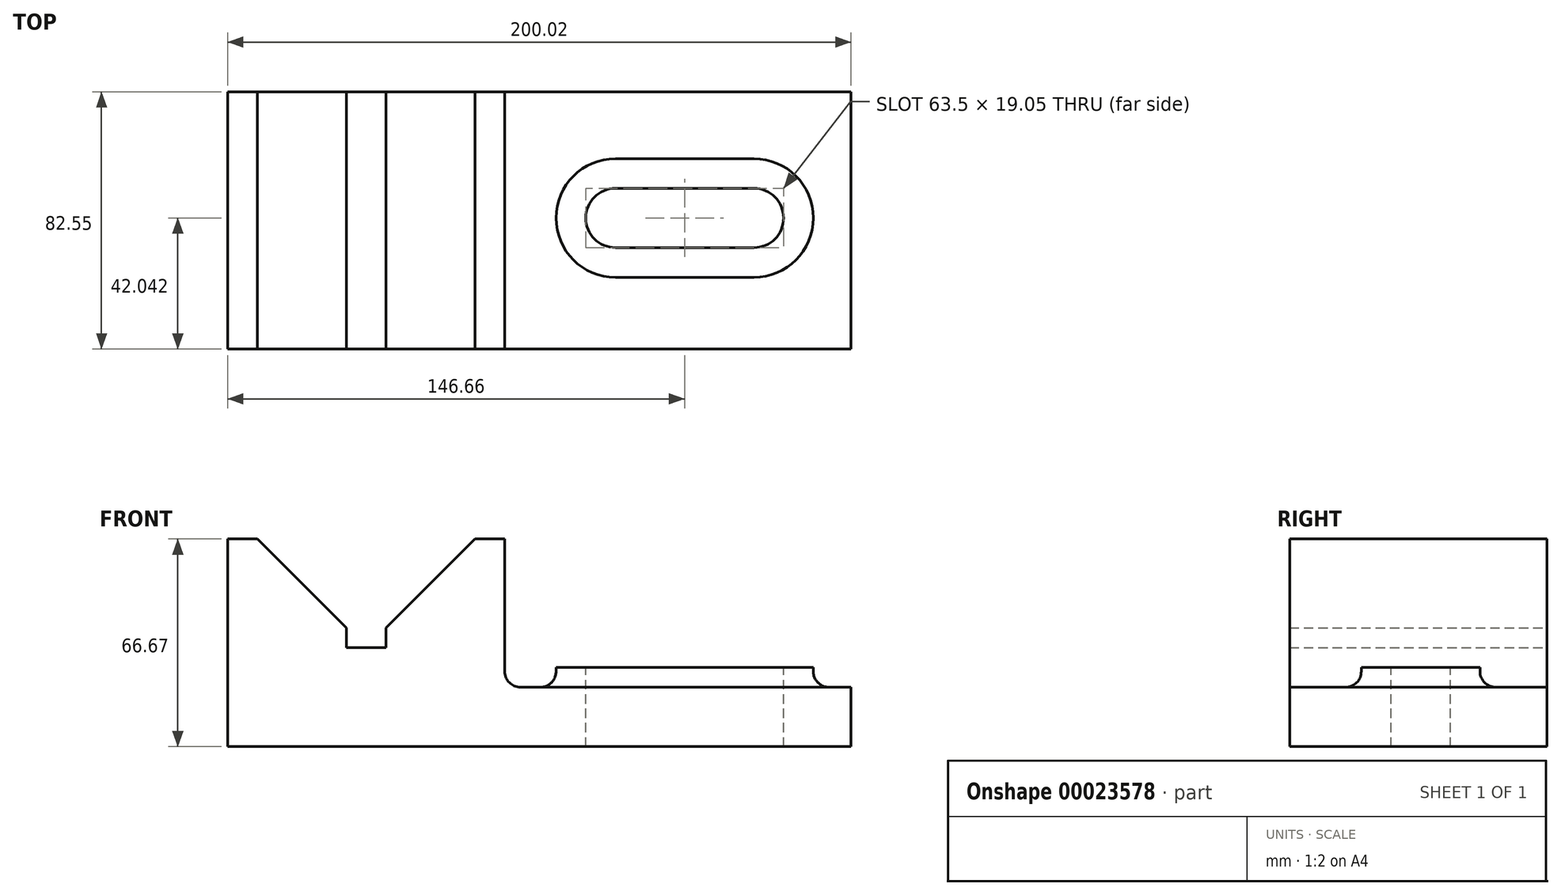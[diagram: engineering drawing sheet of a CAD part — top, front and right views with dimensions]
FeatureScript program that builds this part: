
annotation { "Feature Type Name" : "Feature", "Feature Type Description" : "" }
export const myFeature = defineFeature(function(context is Context, id is Id, definition is map)
    precondition{}
    {
        {
            var Q0;
            Q0=qCreatedBy(makeId("Front.planeOp"),FACE);
            var sketch = newSketch(context, id + "F0", { "sketchPlane" : qUnion([Q0])});
            skLineSegment(sketch, "E0.bottom", {"start": v(-75.58, -32.42) * mm, "end": v(124.44, -32.42) * mm});
            skLineSegment(sketch, "E0.top", {"start": v(-75.58, -51.47) * mm, "end": v(124.44, -51.47) * mm});
            skLineSegment(sketch, "E0.left", {"start": v(-75.58, -32.42) * mm, "end": v(-75.58, -51.47) * mm});
            skLineSegment(sketch, "E0.right", {"start": v(124.44, -32.42) * mm, "end": v(124.44, -51.47) * mm});
            skLineSegment(sketch, "E1.bottom", {"start": v(-75.58, -32.42) * mm, "end": v(-75.58, -32.42) * mm});
            skLineSegment(sketch, "E1.top", {"start": v(-75.58, -51.47) * mm, "end": v(-75.58, -51.47) * mm});
            skLineSegment(sketch, "E2.bottom", {"start": v(-75.58, -51.47) * mm, "end": v(13.32, -51.47) * mm});
            skLineSegment(sketch, "E2.left", {"start": v(-75.58, -51.47) * mm, "end": v(-75.58, 15.2) * mm});
            skLineSegment(sketch, "E2.right", {"start": v(13.32, -51.47) * mm, "end": v(13.32, 15.2) * mm});
            skLineSegment(sketch, "E3", {"start": v(-66.06, 15.2) * mm, "end": v(-37.48, -13.37) * mm});
            skLineSegment(sketch, "E4", {"start": v(-37.48, -13.37) * mm, "end": v(-37.48, -19.72) * mm});
            skLineSegment(sketch, "E5", {"start": v(-37.48, -19.72) * mm, "end": v(-24.78, -19.72) * mm});
            skLineSegment(sketch, "E6", {"start": v(-24.78, -19.72) * mm, "end": v(-24.78, -13.37) * mm});
            skLineSegment(sketch, "E7", {"start": v(-24.78, -13.37) * mm, "end": v(3.8, 15.2) * mm});
            skLineSegment(sketch, "E8.trimOffspring", {"start": v(3.8, 15.2) * mm, "end": v(13.32, 15.2) * mm});
            skLineSegment(sketch, "E9", {"start": v(-75.58, 15.2) * mm, "end": v(-66.06, 15.2) * mm});
            skSolve(sketch);
        }
        {
            var Q0;
            Q0 = qSketchRegion(id + "F0", true);
            extrude(context, id + "F1", {"entities" : qUnion([Q0]), "depth" : 82.55 * mm});
        }
        {
            var Q0;
            Q0=qCreatedBy(makeId("Top.planeOp"),FACE);
            var sketch = newSketch(context, id + "F2", { "sketchPlane" : qUnion([Q0])});
            skLineSegment(sketch, "E10.bottom", {"start": v(48.86, -30.98) * mm, "end": v(93.3, -30.98) * mm});
            skLineSegment(sketch, "E10.top", {"start": v(48.86, -50.03) * mm, "end": v(93.3, -50.03) * mm});
            skArc(sketch, "E11", {"start": v(48.86, -30.98) * mm, "mid": v(39.33, -40.5) * mm, "end": v(48.86, -50.03) * mm});
            skArc(sketch, "E12", {"start": v(93.3, -50.03) * mm, "mid": v(102.83, -40.5) * mm, "end": v(93.3, -30.98) * mm});
            skLineSegment(sketch, "E13.bottom", {"start": v(48.86, -59.56) * mm, "end": v(93.3, -59.56) * mm});
            skArc(sketch, "E14", {"start": v(93.3, -59.56) * mm, "mid": v(112.36, -40.5) * mm, "end": v(93.3, -21.46) * mm});
            skArc(sketch, "E15", {"start": v(48.86, -21.46) * mm, "mid": v(29.8, -40.5) * mm, "end": v(48.86, -59.56) * mm});
            skLineSegment(sketch, "E16", {"start": v(48.86, -21.46) * mm, "end": v(93.3, -21.46) * mm});
            skSolve(sketch);
        }
        {
            var Q0;
            Q0=makeQuery(id+"F2.imprint","IMPRINT",FACE,{"disambiguationData":[TD([[makeQuery(id+"F2.imprint","IMPRINT",EDGE,{"derivedFrom":sQuery(id+"F2.wireOp",EDGE,"E10.bottom")}),1.0]])]});
            extrude(context, id + "F3", {"entities" : qUnion([Q0]), "operationType" : NewBodyOperationType.ADD, "oppositeDirection" : true, "depth" : 38.1 * mm});
        }
        {
            var Q0;
            Q0=makeQuery(id+"F3.opExtrude","CAP_FACE",FACE,{"disambiguationData":[OSD([sQuery(id+"F2.wireOp",EDGE,"E10.bottom"),sQuery(id+"F2.wireOp",EDGE,"E10.top"),sQuery(id+"F2.wireOp",EDGE,"E11"),sQuery(id+"F2.wireOp",EDGE,"E12"),sQuery(id+"F2.wireOp",EDGE,"E13.bottom"),sQuery(id+"F2.wireOp",EDGE,"E14"),sQuery(id+"F2.wireOp",EDGE,"E15"),sQuery(id+"F2.wireOp",EDGE,"E16")])],"isStart":true});
            extrude(context, id + "F4", {"entities" : qUnion([Q0]), "operationType" : NewBodyOperationType.REMOVE, "oppositeDirection" : true, "depth" : 32.36 * mm});
        }
        {
            var Q0;
            Q0=makeQuery(id+"F4.boolean.opBoolean","COPY",FACE,{"derivedFrom":makeQuery(id+"F4.opExtrude","CAP_FACE",FACE,{"disambiguationData":[OSD([sQuery(id+"F2.wireOp",EDGE,"E10.bottom"),sQuery(id+"F2.wireOp",EDGE,"E10.top"),sQuery(id+"F2.wireOp",EDGE,"E11"),sQuery(id+"F2.wireOp",EDGE,"E12"),sQuery(id+"F2.wireOp",EDGE,"E13.bottom"),sQuery(id+"F2.wireOp",EDGE,"E14"),sQuery(id+"F2.wireOp",EDGE,"E15"),sQuery(id+"F2.wireOp",EDGE,"E16")])],"isStart":false})});
            extrude(context, id + "F5", {"entities" : qUnion([Q0]), "operationType" : NewBodyOperationType.ADD, "depth" : 6.35 * mm});
        }
        {
            var Q0;
            Q0=makeQuery(id+"F1.opExtrude","SWEPT_EDGE",EDGE,{"disambiguationData":[OSD([sQuery(id+"F0.wireOp",EDGE,"E0.bottom"),sQuery(id+"F0.wireOp",EDGE,"E2.right")])]});
            fillet(context, id + "F6", {"entities" : qUnion([Q0]), "radius" : 5.08 * mm, "tangentPropagation" : true, "allowEdgeOverflow" : false});
        }
        {
            var Q0;
            Q0=makeQuery(id+"F3.boolean.opBoolean","SPLIT",FACE,{"disambiguationData":[TD([makeQuery(id+"F3.opExtrude","SWEPT_FACE",FACE,{"disambiguationData":[OSD([sQuery(id+"F2.wireOp",EDGE,"E10.bottom")])]})])],"derivedFrom":makeQuery(id+"F1.opExtrude","SWEPT_FACE",FACE,{"disambiguationData":[OSD([sQuery(id+"F0.wireOp",EDGE,"E0.bottom")])]})});
            extrude(context, id + "F7", {"entities" : qUnion([Q0]), "operationType" : NewBodyOperationType.REMOVE, "oppositeDirection" : true, "depth" : 2514.6 * mm});
        }
        {
            var Q0;
            Q0=makeQuery(id+"F3.boolean.opBoolean","INTERSECT",EDGE,{"derivedFrom":[makeQuery(id+"F1.opExtrude","SWEPT_FACE",FACE,{"disambiguationData":[OSD([sQuery(id+"F0.wireOp",EDGE,"E0.bottom")])]}),makeQuery(id+"F3.opExtrude","SWEPT_FACE",FACE,{"disambiguationData":[OSD([sQuery(id+"F2.wireOp",EDGE,"E14")])]})]});
            var Q1;
            Q1=makeQuery(id+"F3.boolean.opBoolean","INTERSECT",EDGE,{"derivedFrom":[makeQuery(id+"F1.opExtrude","SWEPT_FACE",FACE,{"disambiguationData":[OSD([sQuery(id+"F0.wireOp",EDGE,"E0.bottom")])]}),makeQuery(id+"F3.opExtrude","SWEPT_FACE",FACE,{"disambiguationData":[OSD([sQuery(id+"F2.wireOp",EDGE,"E13.bottom")])]})]});
            var Q2;
            Q2=makeQuery(id+"F3.boolean.opBoolean","INTERSECT",EDGE,{"derivedFrom":[makeQuery(id+"F1.opExtrude","SWEPT_FACE",FACE,{"disambiguationData":[OSD([sQuery(id+"F0.wireOp",EDGE,"E0.bottom")])]}),makeQuery(id+"F3.opExtrude","SWEPT_FACE",FACE,{"disambiguationData":[OSD([sQuery(id+"F2.wireOp",EDGE,"E15")])]})]});
            fillet(context, id + "F8", {"entities" : qUnion([Q0, Q1, Q2]), "radius" : 5.08 * mm, "tangentPropagation" : true, "allowEdgeOverflow" : false});
        }
    });
